# Revit family: LTV8HS
name_source: partatom
category: Lighting Fixtures
revit_build: Autodesk Revit 2014 (Build: 20130308_1515(x64)
units: mm (PartAtom-declared; Revit-internal decimal feet)

## types (2) — shared parameters
Apparent Load = 0 VA
Certification = UL 1598 Standard for Luminaires.
■ UL 8750 Standard for Safety for Light
Emitting Diode (LED) Equipment for use
in Lighting Products.
Color Filter = 16777215
Default Elevation = 48.000"
Description = RGBW Color Changing via Bluetooth® or DMX. The Lightvault 8 RGBW Half Shield directs light while hiding glare and is well suited for controlling light in pedestrian areas and restaurants.
Dimming Lamp Color Temperature Shift = <None>
Emit Shape Visible in Rendering = No
Features = Bluetooth connectivity for remote control aiming, dimming, color changing
Free mobile App for Adroid and iOS
X-Y tilt controls for aiming 12° in any direction
Variable dimming to 20% in 1% increments
IP68 sealed maintenance free LED light engine
Two sizes: Medium 10 inch, Large 13 inch
Finish = Bronze
Lamp = LED
Lens = White Glass
Manufacturer = Kim Lighting
Material = Plastic - Black
Model = Lightvault® 8 RGBW Half Shield
Nominal Watts = 31 W
Photometric Web File = ltv81ff-nf-36l3k.ies
Product Documentation Link = https://hubbellcdn.com
Product Page URL = https://www.hubbell.com
Tilt Angle = 60.00°
URL = https://www.hubbell.com
Voltage = 120 V
Warranty = For full warranty see http://www.
hubbelllighting.com/resources/warranty
■ Opening of Component Module on site will
void warranty

## per-type parameters (varying)
| type | Depth | Diameter | Emit from Circle Diameter | Fixture | Radius |
| LTV81HS | 10.000" | 13.000" | 13.000" | LTV8 : LTV81HS | 6.500" |
| LTV82HS | 9.875" | 10.000" | 10.000" | LTV8 : LTV82HS | 5.000" |

## geometry (parser evidence)
native form markers: Blend x18, Sweep x4
no freeform markers — native parametric forms only
